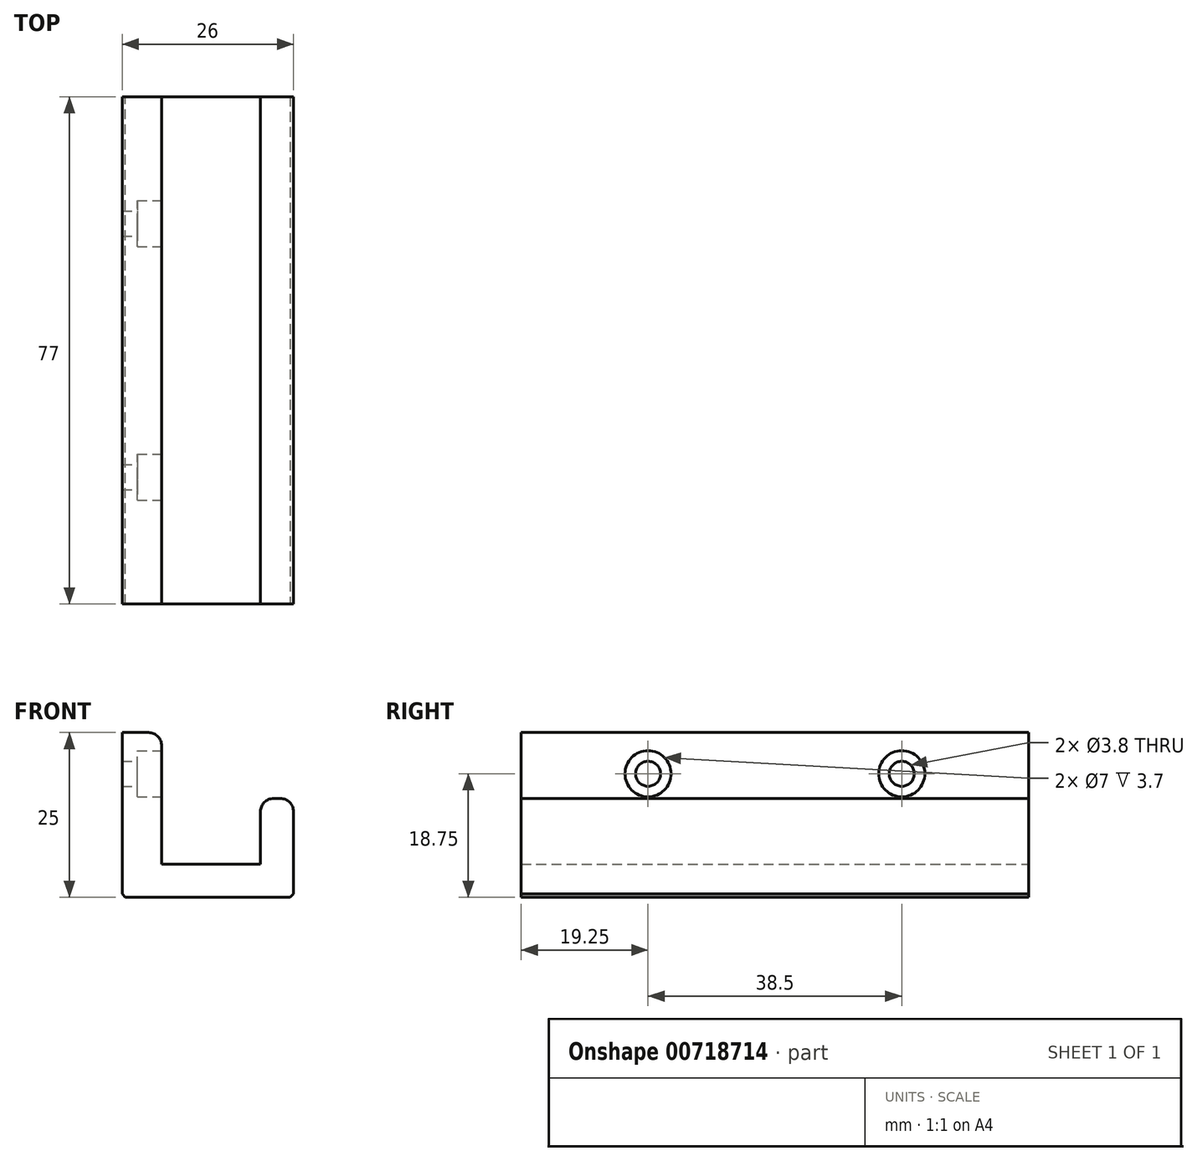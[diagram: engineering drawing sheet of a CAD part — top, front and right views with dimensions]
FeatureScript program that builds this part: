
annotation { "Feature Type Name" : "Feature", "Feature Type Description" : "" }
export const myFeature = defineFeature(function(context is Context, id is Id, definition is map)
    precondition{}
    {
        {
            var Q0;
            Q0=qCreatedBy(makeId("Front.planeOp"),FACE);
            var sketch = newSketch(context, id + "F0", { "sketchPlane" : qUnion([Q0])});
            skLineSegment(sketch, "E0.bottom", {"start": v(0, 0) * mm, "end": v(7.5, 0) * mm});
            skLineSegment(sketch, "E0.top", {"start": v(0, 5) * mm, "end": v(7.5, 5) * mm});
            skLineSegment(sketch, "E0.left", {"start": v(0, 0) * mm, "end": v(0, 5) * mm});
            skLineSegment(sketch, "E0.right", {"start": v(7.5, 0) * mm, "end": v(7.5, 5) * mm});
            skLineSegment(sketch, "E1.MirrorCS", {"start": v(0, 5) * mm, "end": v(-7.5, 5) * mm});
            skLineSegment(sketch, "E2.MirrorCS", {"start": v(-7.5, 0) * mm, "end": v(-7.5, 5) * mm});
            skLineSegment(sketch, "E3.MirrorCS", {"start": v(0, 0) * mm, "end": v(-7.5, 0) * mm});
            skLineSegment(sketch, "E4", {"start": v(7.5, 5) * mm, "end": v(7.5, 15) * mm});
            skLineSegment(sketch, "E5", {"start": v(7.5, 15) * mm, "end": v(12.5, 15) * mm});
            skLineSegment(sketch, "E6", {"start": v(12.5, 15) * mm, "end": v(12.5, 0) * mm});
            skLineSegment(sketch, "E7", {"start": v(12.5, 0) * mm, "end": v(7.5, 0) * mm});
            skLineSegment(sketch, "E8.bottom", {"start": v(-7.5, 0) * mm, "end": v(-13.5, 0) * mm});
            skLineSegment(sketch, "E8.top", {"start": v(-7.5, 25) * mm, "end": v(-13.5, 25) * mm});
            skLineSegment(sketch, "E8.left", {"start": v(-7.5, 0) * mm, "end": v(-7.5, 25) * mm});
            skLineSegment(sketch, "E8.right", {"start": v(-13.5, 0) * mm, "end": v(-13.5, 25) * mm});
            skSolve(sketch);
        }
        {
            var Q0;
            Q0=qSketchRegion(id+"F0",true);
            extrude(context, id + "F1", {"entities" : qUnion([Q0]), "endBound" : BoundingType.SYMMETRIC, "depth" : 77 * mm, "offsetDistance" : 25 * mm});
        }
        {
            var Q0;
            Q0=makeQuery(id+"F1.opExtrude","SWEPT_FACE",FACE,{"disambiguationData":[OSD([sQuery(id+"F0.wireOp",EDGE,"E8.left")])]});
            var sketch = newSketch(context, id + "F2", { "sketchPlane" : qUnion([Q0])});
            skLineSegment(sketch, "E9", {"start": v(0, 0) * mm, "end": v(0, 25) * mm});
            skLineSegment(sketch, "E10", {"start": v(0, 25) * mm, "end": v(0, 12.5) * mm});
            skLineSegment(sketch, "E11", {"start": v(0, 12.5) * mm, "end": v(0, 18.75) * mm});
            skLineSegment(sketch, "E12", {"start": v(0, 18.75) * mm, "end": v(38.5, 18.75) * mm});
            skLineSegment(sketch, "E13", {"start": v(0, 18.75) * mm, "end": v(-38.5, 18.75) * mm});
            skPoint(sketch, "E14", {"position": v(-19.25, 18.75) * mm});
            skPoint(sketch, "E15", {"position": v(19.25, 18.75) * mm});
            skSolve(sketch);
        }
        {
            var Q0;
            Q0=sQuery(id+"F2.wireOp",VERTEX,"E14");
            var Q1;
            Q1=sQuery(id+"F2.wireOp",VERTEX,"E15");
            var Q2;
            Q2=makeQuery(id+"F1.opExtrude","SWEPT_BODY",BODY,{"disambiguationData":[OSD([sQuery(id+"F0.wireOp",EDGE,"E0.bottom"),sQuery(id+"F0.wireOp",EDGE,"E0.top"),sQuery(id+"F0.wireOp",EDGE,"E1.MirrorCS"),sQuery(id+"F0.wireOp",EDGE,"E3.MirrorCS"),sQuery(id+"F0.wireOp",EDGE,"E4"),sQuery(id+"F0.wireOp",EDGE,"E5"),sQuery(id+"F0.wireOp",EDGE,"E6"),sQuery(id+"F0.wireOp",EDGE,"E7"),sQuery(id+"F0.wireOp",EDGE,"E8.bottom"),sQuery(id+"F0.wireOp",EDGE,"E8.top"),sQuery(id+"F0.wireOp",EDGE,"E8.left"),sQuery(id+"F0.wireOp",EDGE,"E8.right")])]});
            hole(context, id + "F3", {"style" : HoleStyle.C_BORE, "endStyle" : HoleEndStyle.BLIND, "holeDiameter" : 3.8 * mm, "cBoreDiameter" : 7 * mm, "cBoreDepth" : 3.7 * mm, "majorDiameter" : 5 * mm, "holeDepth" : 6 * mm, "isTappedThrough" : true, "tappedDepth" : 12 * mm, "tapClearance" : 3, "locations" : qUnion([Q0, Q1]), "scope" : qUnion([Q2])});
        }
        {
            var Q0;
            Q0=makeQuery(id+"F1.opExtrude","SWEPT_EDGE",EDGE,{"disambiguationData":[OSD([sQuery(id+"F0.wireOp",EDGE,"E5"),sQuery(id+"F0.wireOp",EDGE,"E6")])]});
            var Q1;
            Q1=makeQuery(id+"F1.opExtrude","SWEPT_EDGE",EDGE,{"disambiguationData":[OSD([sQuery(id+"F0.wireOp",EDGE,"E4"),sQuery(id+"F0.wireOp",EDGE,"E5")])]});
            var Q2;
            Q2=makeQuery(id+"F1.opExtrude","SWEPT_EDGE",EDGE,{"disambiguationData":[OSD([sQuery(id+"F0.wireOp",EDGE,"E8.top"),sQuery(id+"F0.wireOp",EDGE,"E8.left")])]});
            fillet(context, id + "F4", {"entities" : qUnion([Q0, Q1, Q2]), "radius" : 2 * mm, "tangentPropagation" : true, "allowEdgeOverflow" : false});
        }
        {
            var Q0;
            Q0=makeQuery(id+"F1.opExtrude","SWEPT_EDGE",EDGE,{"disambiguationData":[OSD([sQuery(id+"F0.wireOp",EDGE,"E6"),sQuery(id+"F0.wireOp",EDGE,"E7")])]});
            var Q1;
            Q1=makeQuery(id+"F1.opExtrude","SWEPT_EDGE",EDGE,{"disambiguationData":[OSD([sQuery(id+"F0.wireOp",EDGE,"E8.bottom"),sQuery(id+"F0.wireOp",EDGE,"E8.right")])]});
            chamfer(context, id + "F5", {"entities" : qUnion([Q0, Q1]), "width" : .5 * mm, "tangentPropagation" : true});
        }
    });
